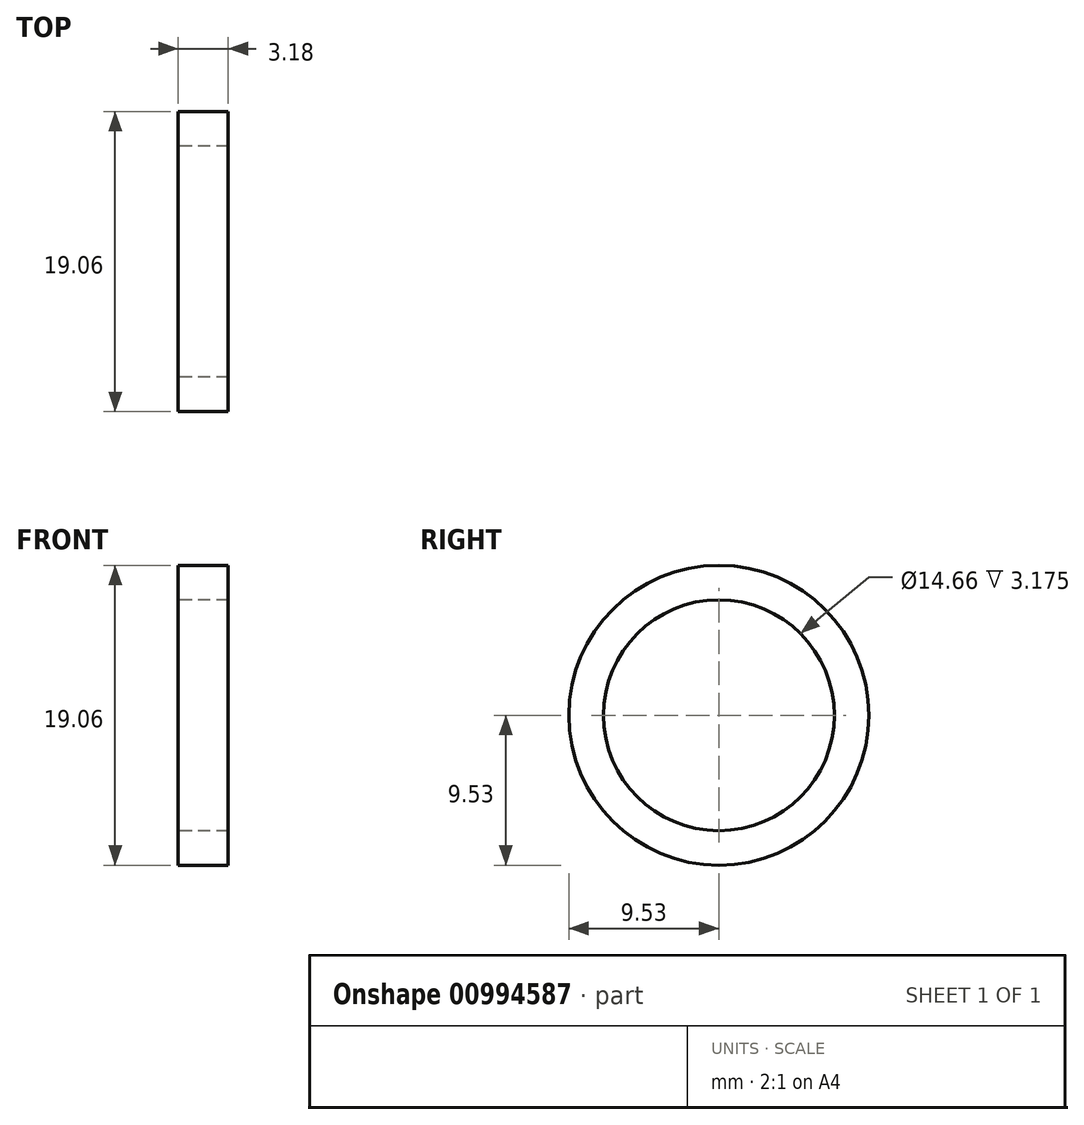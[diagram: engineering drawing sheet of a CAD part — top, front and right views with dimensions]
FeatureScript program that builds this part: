
annotation { "Feature Type Name" : "Feature", "Feature Type Description" : "" }
export const myFeature = defineFeature(function(context is Context, id is Id, definition is map)
    precondition{}
    {
        {
            var Q0;
            Q0=qCreatedBy(makeId("Right.planeOp"),FACE);
            var sketch = newSketch(context, id + "F0", { "sketchPlane" : qUnion([Q0])});
            skCircle(sketch, "E0", {"center": v(0, 0) * mm, "radius": 9.53 * mm});
            skCircle(sketch, "E1", {"center": v(0, 0) * mm, "radius": 7.33 * mm});
            skCircle(sketch, "E2.cCircle", {"center": v(0, 0) * mm, "radius": 6.35 * mm, "construction": true});
            skLineSegment(sketch, "E2.0", {"start": v(-6.35, -3.67) * mm, "end": v(-6.35, 3.67) * mm, "construction": true});
            skLineSegment(sketch, "E2.1", {"start": v(-6.35, 3.67) * mm, "end": v(0, 7.33) * mm, "construction": true});
            skLineSegment(sketch, "E2.2", {"start": v(0, 7.33) * mm, "end": v(6.35, 3.67) * mm, "construction": true});
            skLineSegment(sketch, "E2.3", {"start": v(6.35, 3.67) * mm, "end": v(6.35, -3.67) * mm, "construction": true});
            skLineSegment(sketch, "E2.4", {"start": v(6.35, -3.67) * mm, "end": v(0, -7.33) * mm, "construction": true});
            skLineSegment(sketch, "E2.5", {"start": v(0, -7.33) * mm, "end": v(-6.35, -3.67) * mm, "construction": true});
            skPoint(sketch, "E2.0.midPoint", {"position": v(-6.35, 0) * mm});
            skSolve(sketch);
        }
        {
            var Q0;
            Q0=makeQuery(id+"F0.imprint","IMPRINT",FACE,{"disambiguationData":[TD([[makeQuery(id+"F0.imprint","IMPRINT",EDGE,{"derivedFrom":sQuery(id+"F0.wireOp",EDGE,"E0")}),1.0]])]});
            extrude(context, id + "F1", {"entities" : qUnion([Q0]), "depth" : 3.17 * mm, "offsetDistance" : 25.4 * mm});
        }
    });
